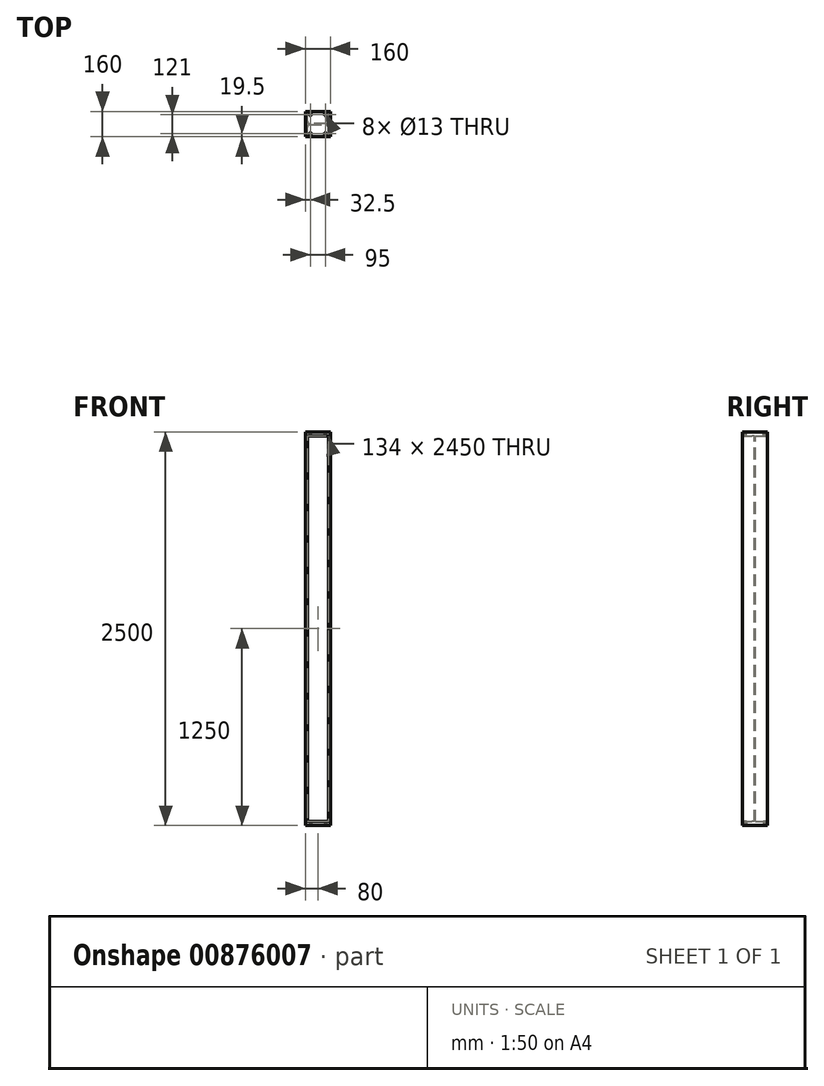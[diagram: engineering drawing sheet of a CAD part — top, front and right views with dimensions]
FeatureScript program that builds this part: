
annotation { "Feature Type Name" : "Feature", "Feature Type Description" : "" }
export const myFeature = defineFeature(function(context is Context, id is Id, definition is map)
    precondition{}
    {
        {
            assignVariable(context, id + "F0", {"name" : "l", "anyValue" : 2500});
        }
        {
            var Q0;
            Q0=qCreatedBy(makeId("Top.planeOp"),FACE);
            var sketch = newSketch(context, id + "F1", { "sketchPlane" : qUnion([Q0])});
            skLineSegment(sketch, "E0", {"start": v(-80, -80) * mm, "end": v(-80, 80) * mm});
            skLineSegment(sketch, "E1", {"start": v(-80, 80) * mm, "end": v(-67, 80) * mm});
            skLineSegment(sketch, "E2", {"start": v(-67, 80) * mm, "end": v(-67, 19) * mm});
            skLineSegment(sketch, "E3", {"start": v(-52, 4) * mm, "end": v(52, 4) * mm});
            skLineSegment(sketch, "E4", {"start": v(67, 19) * mm, "end": v(67, 80) * mm});
            skLineSegment(sketch, "E5", {"start": v(67, 80) * mm, "end": v(80, 80) * mm});
            skLineSegment(sketch, "E6", {"start": v(80, 80) * mm, "end": v(80, -80) * mm});
            skLineSegment(sketch, "E7", {"start": v(80, -80) * mm, "end": v(67, -80) * mm});
            skLineSegment(sketch, "E8", {"start": v(67, -80) * mm, "end": v(67, -19) * mm});
            skLineSegment(sketch, "E9", {"start": v(52, -4) * mm, "end": v(-52, -4) * mm});
            skLineSegment(sketch, "E10", {"start": v(-67, -19) * mm, "end": v(-67, -80) * mm});
            skLineSegment(sketch, "E11", {"start": v(-67, -80) * mm, "end": v(-80, -80) * mm});
            skLineSegment(sketch, "E12", {"start": v(36.95, 0) * mm, "end": v(-50.57, 0) * mm, "construction": true});
            skLineSegment(sketch, "E13", {"start": v(0, 23.47) * mm, "end": v(0, -21.96) * mm, "construction": true});
            skPoint(sketch, "E14.visualSharp", {"position": v(-67, 4) * mm});
            skArc(sketch, "E14.filletArc", {"start": v(-67, 19) * mm, "mid": v(-62.6, 8.4) * mm, "end": v(-52, 4) * mm});
            skPoint(sketch, "E15.visualSharp", {"position": v(67, 4) * mm});
            skArc(sketch, "E15.filletArc", {"start": v(52, 4) * mm, "mid": v(62.6, 8.4) * mm, "end": v(67, 19) * mm});
            skPoint(sketch, "E16.visualSharp", {"position": v(67, -4) * mm});
            skArc(sketch, "E16.filletArc", {"start": v(67, -19) * mm, "mid": v(62.6, -8.4) * mm, "end": v(52, -4) * mm});
            skPoint(sketch, "E17.visualSharp", {"position": v(-67, -4) * mm});
            skArc(sketch, "E17.filletArc", {"start": v(-52, -4) * mm, "mid": v(-62.6, -8.4) * mm, "end": v(-67, -19) * mm});
            skLineSegment(sketch, "E18", {"start": v(-67, 80) * mm, "end": v(67, 80) * mm});
            skLineSegment(sketch, "E19", {"start": v(-67, -80) * mm, "end": v(67, -80) * mm});
            skCircle(sketch, "E20", {"center": v(-47.5, 60.5) * mm, "radius": 6.5 * mm});
            skCircle(sketch, "E21", {"center": v(47.5, 60.5) * mm, "radius": 6.5 * mm});
            skCircle(sketch, "E22", {"center": v(-47.5, -60.5) * mm, "radius": 6.5 * mm});
            skCircle(sketch, "E23", {"center": v(47.5, -60.5) * mm, "radius": 6.5 * mm});
            skLineSegment(sketch, "E24", {"start": v(-47.5, -60.5) * mm, "end": v(47.5, -60.5) * mm, "construction": true});
            skLineSegment(sketch, "E25", {"start": v(47.5, 60.5) * mm, "end": v(47.5, -60.5) * mm, "construction": true});
            skLineSegment(sketch, "E26", {"start": v(-47.5, -60.5) * mm, "end": v(-47.5, 60.5) * mm, "construction": true});
            skLineSegment(sketch, "E27", {"start": v(-47.5, 60.5) * mm, "end": v(47.5, 60.5) * mm, "construction": true});
            skSolve(sketch);
        }
        {
            var Q0;
            Q0=makeQuery(id+"F1.imprint","IMPRINT",FACE,{"disambiguationData":[TD([[makeQuery(id+"F1.imprint","IMPRINT",EDGE,{"derivedFrom":sQuery(id+"F1.wireOp",EDGE,"E0")}),-1.0]])]});
            extrude(context, id + "F2", {"entities" : qUnion([Q0]), "oppositeDirection" : true, "depth" : (0.5 * getVariable(context, 'l')) * mm, "offsetDistance" : 25 * mm});
        }
        {
            var Q0;
            Q0=makeQuery(id+"F1.imprint","IMPRINT",FACE,{"disambiguationData":[TD([[makeQuery(id+"F1.imprint","IMPRINT",EDGE,{"derivedFrom":sQuery(id+"F1.wireOp",EDGE,"E2")}),1.0]])]});
            var Q1;
            Q1=makeQuery(id+"F1.imprint","IMPRINT",FACE,{"disambiguationData":[TD([[makeQuery(id+"F1.imprint","IMPRINT",EDGE,{"derivedFrom":sQuery(id+"F1.wireOp",EDGE,"E0")}),-1.0]])]});
            var Q2;
            Q2=makeQuery(id+"F1.imprint","IMPRINT",FACE,{"disambiguationData":[TD([[makeQuery(id+"F1.imprint","IMPRINT",EDGE,{"derivedFrom":sQuery(id+"F1.wireOp",EDGE,"E8")}),1.0]])]});
            extrude(context, id + "F3", {"entities" : qUnion([Q0, Q1, Q2]), "operationType" : NewBodyOperationType.ADD, "oppositeDirection" : true, "depth" : 25 * mm, "offsetDistance" : 25 * mm});
        }
        {
            var Q0;
            Q0=makeQuery(id+"F2.opExtrude","SWEPT_BODY",BODY,{"disambiguationData":[OSD([sQuery(id+"F1.wireOp",EDGE,"E0"),sQuery(id+"F1.wireOp",EDGE,"E1"),sQuery(id+"F1.wireOp",EDGE,"E2"),sQuery(id+"F1.wireOp",EDGE,"E3"),sQuery(id+"F1.wireOp",EDGE,"E4"),sQuery(id+"F1.wireOp",EDGE,"E5"),sQuery(id+"F1.wireOp",EDGE,"E6"),sQuery(id+"F1.wireOp",EDGE,"E7"),sQuery(id+"F1.wireOp",EDGE,"E8"),sQuery(id+"F1.wireOp",EDGE,"E9"),sQuery(id+"F1.wireOp",EDGE,"E10"),sQuery(id+"F1.wireOp",EDGE,"E11"),sQuery(id+"F1.wireOp",EDGE,"E14.filletArc"),sQuery(id+"F1.wireOp",EDGE,"E15.filletArc"),sQuery(id+"F1.wireOp",EDGE,"E16.filletArc"),sQuery(id+"F1.wireOp",EDGE,"E17.filletArc")])]});
            var Q1;
            Q1=makeQuery(id+"F2.opExtrude","CAP_FACE",FACE,{"disambiguationData":[OSD([sQuery(id+"F1.wireOp",EDGE,"E0"),sQuery(id+"F1.wireOp",EDGE,"E1"),sQuery(id+"F1.wireOp",EDGE,"E2"),sQuery(id+"F1.wireOp",EDGE,"E3"),sQuery(id+"F1.wireOp",EDGE,"E4"),sQuery(id+"F1.wireOp",EDGE,"E5"),sQuery(id+"F1.wireOp",EDGE,"E6"),sQuery(id+"F1.wireOp",EDGE,"E7"),sQuery(id+"F1.wireOp",EDGE,"E8"),sQuery(id+"F1.wireOp",EDGE,"E9"),sQuery(id+"F1.wireOp",EDGE,"E10"),sQuery(id+"F1.wireOp",EDGE,"E11"),sQuery(id+"F1.wireOp",EDGE,"E14.filletArc"),sQuery(id+"F1.wireOp",EDGE,"E15.filletArc"),sQuery(id+"F1.wireOp",EDGE,"E16.filletArc"),sQuery(id+"F1.wireOp",EDGE,"E17.filletArc")])],"isStart":false});
            mirror(context, id + "F4", {"operationType" : NewBodyOperationType.ADD, "entities" : qUnion([Q0]), "mirrorPlane" : qUnion([Q1])});
        }
    });
